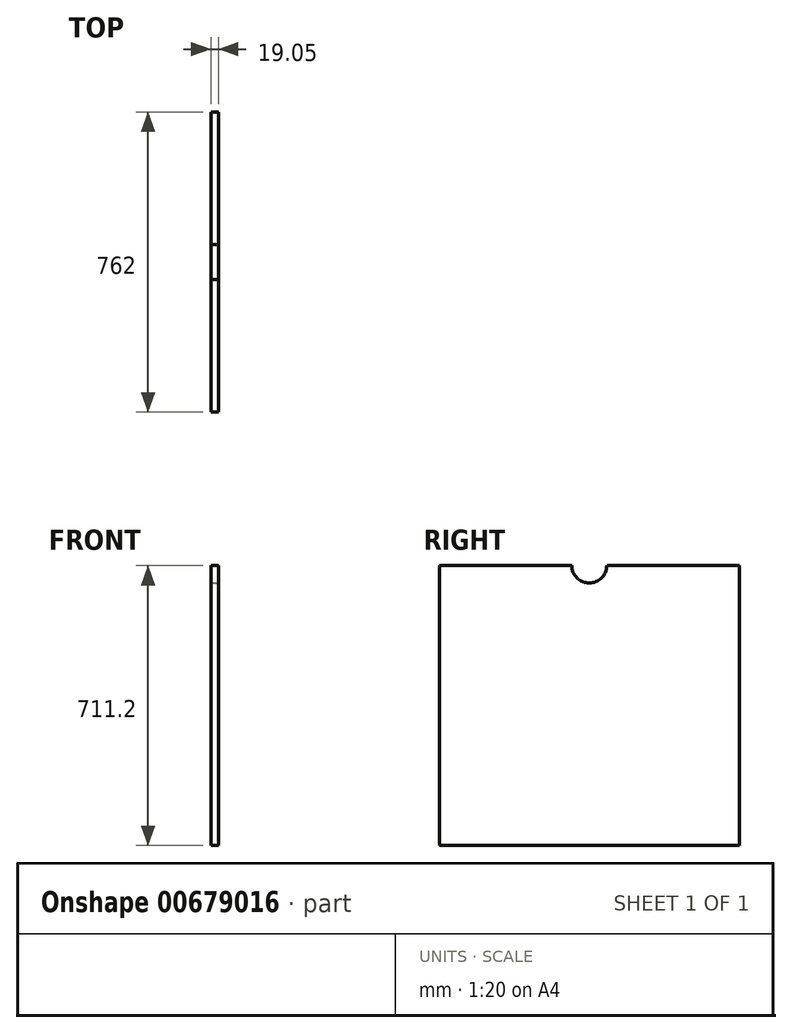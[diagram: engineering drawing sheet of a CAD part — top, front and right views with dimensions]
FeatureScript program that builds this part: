
annotation { "Feature Type Name" : "Feature", "Feature Type Description" : "" }
export const myFeature = defineFeature(function(context is Context, id is Id, definition is map)
    precondition{}
    {
        {
            var Q0;
            Q0=qCreatedBy(makeId("Right.planeOp"),FACE);
            var sketch = newSketch(context, id + "F0", { "sketchPlane" : qUnion([Q0])});
            skLineSegment(sketch, "E0.bottom", {"start": v(381, 355.6) * mm, "end": v(-381, 355.6) * mm});
            skLineSegment(sketch, "E0.top", {"start": v(381, -355.6) * mm, "end": v(-381, -355.6) * mm});
            skLineSegment(sketch, "E0.left", {"start": v(381, 355.6) * mm, "end": v(381, -355.6) * mm});
            skLineSegment(sketch, "E0.right", {"start": v(-381, 355.6) * mm, "end": v(-381, -355.6) * mm});
            skPoint(sketch, "E0.middle", {"position": v(0, 0) * mm});
            skSolve(sketch);
        }
        {
            var Q0;
            Q0=makeQuery(id+"F0.imprint","IMPRINT",FACE,{"disambiguationData":[TD([[makeQuery(id+"F0.imprint","IMPRINT",EDGE,{"derivedFrom":sQuery(id+"F0.wireOp",EDGE,"E0.bottom")}),1.0]])]});
            extrude(context, id + "F1", {"entities" : qUnion([Q0]), "depth" : 19.05 * mm, "offsetDistance" : 25.4 * mm});
        }
        {
            var Q0;
            Q0=makeQuery(id+"F1.opExtrude","CAP_FACE",FACE,{"disambiguationData":[OSD([sQuery(id+"F0.wireOp",EDGE,"E0.bottom"),sQuery(id+"F0.wireOp",EDGE,"E0.top"),sQuery(id+"F0.wireOp",EDGE,"E0.left"),sQuery(id+"F0.wireOp",EDGE,"E0.right")])],"isStart":false});
            var sketch = newSketch(context, id + "F2", { "sketchPlane" : qUnion([Q0])});
            skCircle(sketch, "E1", {"center": v(0, 355.6) * mm, "radius": 44.45 * mm});
            skSolve(sketch);
        }
        {
            var Q0;
            {var subQ0=sQuery(id+"F2.wireOp",EDGE,"E1");var subQ1=makeQuery(id+"F1.opExtrude","CAP_EDGE",EDGE,{"disambiguationData":[OSD([sQuery(id+"F0.wireOp",EDGE,"E0.bottom")])],"isStart":false});var subQ2=makeQuery(id+"F2.imprint","INTERSECT",VERTEX,{"disambiguationData":[OD(0.0)],"derivedFrom":[subQ1,subQ0]});Q0=makeQuery(id+"F2.imprint","IMPRINT",FACE,{"disambiguationData":[TD([[makeQuery(id+"F2.imprint","IMPRINT",EDGE,{"disambiguationData":[TD([[subQ2,1.0]])],"derivedFrom":subQ0}),1.0]])]});}
            extrude(context, id + "F3", {"entities" : qUnion([Q0]), "operationType" : NewBodyOperationType.REMOVE, "oppositeDirection" : true, "depth" : 25.4 * mm, "offsetDistance" : 25.4 * mm});
        }
    });
